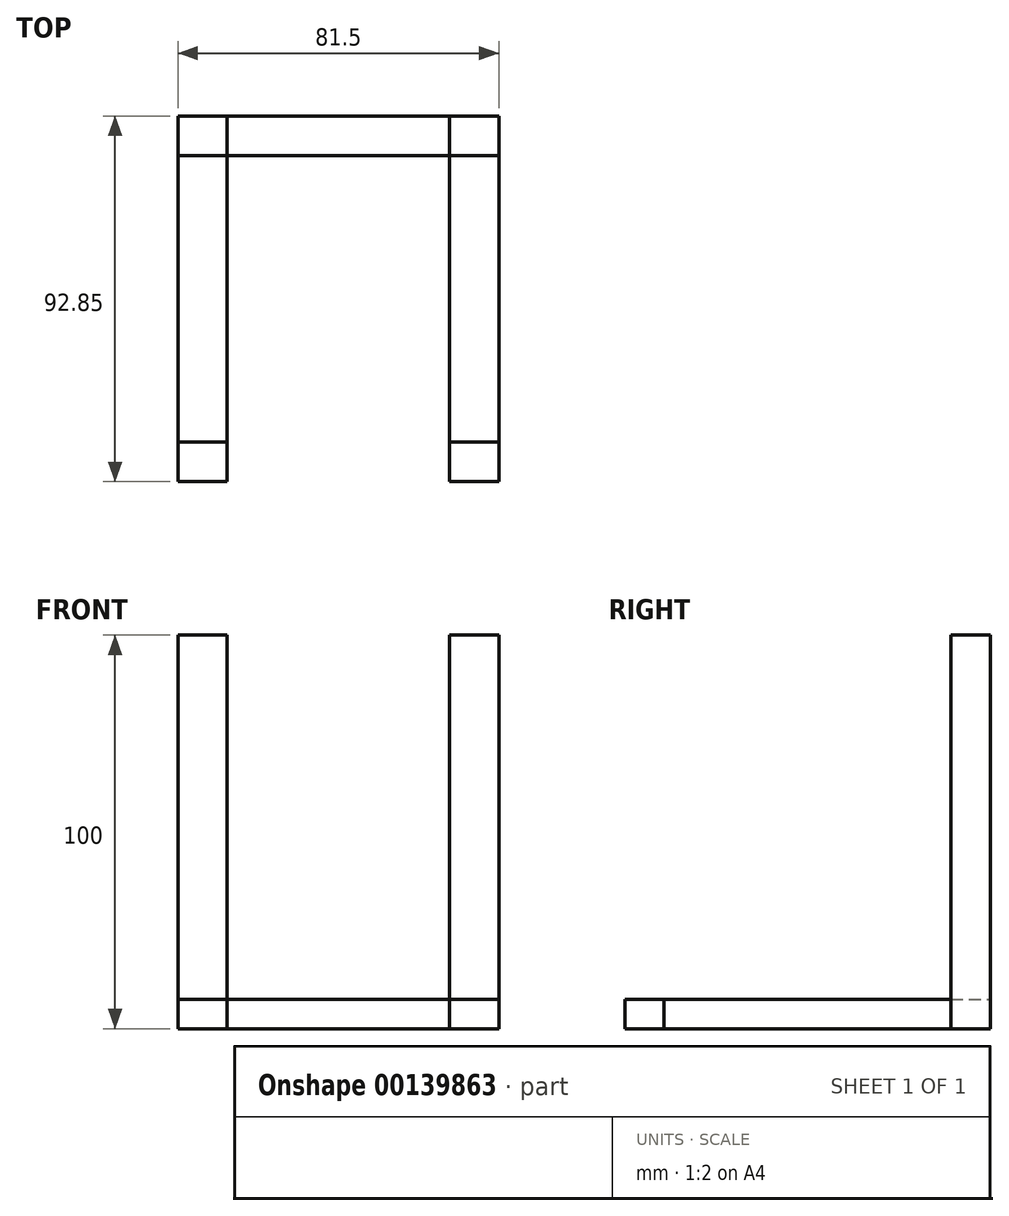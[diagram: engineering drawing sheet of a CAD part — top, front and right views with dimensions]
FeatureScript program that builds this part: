
annotation { "Feature Type Name" : "Feature", "Feature Type Description" : "" }
export const myFeature = defineFeature(function(context is Context, id is Id, definition is map)
    precondition{}
    {
        {
            var Q0;
            Q0=qCreatedBy(makeId("Top.planeOp"),FACE);
            var sketch = newSketch(context, id + "F0", { "sketchPlane" : qUnion([Q0])});
            skLineSegment(sketch, "E0", {"start": v(-34.4, 34.84) * mm, "end": v(47.1, 34.84) * mm});
            skLineSegment(sketch, "E1", {"start": v(47.1, 34.84) * mm, "end": v(47.1, -58.01) * mm});
            skLineSegment(sketch, "E2", {"start": v(47.1, -58.01) * mm, "end": v(-34.4, -58.01) * mm});
            skLineSegment(sketch, "E3", {"start": v(-34.4, -58.01) * mm, "end": v(-34.4, 34.84) * mm});
            skLineSegment(sketch, "E4", {"start": v(-34.4, 24.84) * mm, "end": v(-21.9, 24.84) * mm});
            skLineSegment(sketch, "E5", {"start": v(-21.9, 24.84) * mm, "end": v(-21.9, 34.84) * mm});
            skLineSegment(sketch, "E6", {"start": v(34.6, 34.84) * mm, "end": v(34.6, 24.84) * mm});
            skLineSegment(sketch, "E7", {"start": v(34.6, 24.84) * mm, "end": v(47.1, 24.84) * mm});
            skLineSegment(sketch, "E8", {"start": v(47.1, -48.01) * mm, "end": v(34.6, -48.01) * mm});
            skLineSegment(sketch, "E9", {"start": v(34.6, -48.01) * mm, "end": v(34.6, -58.01) * mm});
            skLineSegment(sketch, "E10", {"start": v(-34.4, -48.01) * mm, "end": v(-21.9, -48.01) * mm});
            skLineSegment(sketch, "E11", {"start": v(-21.9, -48.01) * mm, "end": v(-21.9, -58.01) * mm});
            skLineSegment(sketch, "E12", {"start": v(-21.9, 24.84) * mm, "end": v(-21.9, -48.01) * mm});
            skLineSegment(sketch, "E13", {"start": v(34.6, -48.01) * mm, "end": v(34.6, 24.84) * mm});
            skLineSegment(sketch, "E14", {"start": v(-21.9, 24.84) * mm, "end": v(34.6, 24.84) * mm});
            skSolve(sketch);
        }
        {
            var Q0;
            {var subQ4=sQuery(id+"F0.wireOp",EDGE,"E4");Q0=makeQuery(id+"F0.imprint","IMPRINT",FACE,{"disambiguationData":[TD([[makeQuery(id+"F0.imprint","IMPRINT",EDGE,{"derivedFrom":subQ4}),1.0]])]});}
            var Q1;
            {var subQ3=sQuery(id+"F0.wireOp",EDGE,"E6");Q1=makeQuery(id+"F0.imprint","IMPRINT",FACE,{"disambiguationData":[TD([[makeQuery(id+"F0.imprint","IMPRINT",EDGE,{"derivedFrom":subQ3}),1.0]])]});}
            extrude(context, id + "F1", {"entities" : qUnion([Q0, Q1]), "depth" : 100 * mm});
        }
        {
            var Q0;
            {var subQ0=sQuery(id+"F0.wireOp",EDGE,"E4");Q0=makeQuery(id+"F0.imprint","IMPRINT",FACE,{"disambiguationData":[TD([[makeQuery(id+"F0.imprint","IMPRINT",EDGE,{"derivedFrom":subQ0}),-1.0]])]});}
            var Q1;
            {var subQ0=sQuery(id+"F0.wireOp",EDGE,"E7");Q1=makeQuery(id+"F0.imprint","IMPRINT",FACE,{"disambiguationData":[TD([[makeQuery(id+"F0.imprint","IMPRINT",EDGE,{"derivedFrom":subQ0}),-1.0]])]});}
            var Q2;
            {var subQ0=sQuery(id+"F0.wireOp",EDGE,"E5");Q2=makeQuery(id+"F0.imprint","IMPRINT",FACE,{"disambiguationData":[TD([[makeQuery(id+"F0.imprint","IMPRINT",EDGE,{"derivedFrom":subQ0}),-1.0]])]});}
            extrude(context, id + "F2", {"entities" : qUnion([Q0, Q1, Q2]), "depth" : 7.5 * mm});
        }
        {
            var Q0;
            {var subQ4=sQuery(id+"F0.wireOp",EDGE,"E10");Q0=makeQuery(id+"F0.imprint","IMPRINT",FACE,{"disambiguationData":[TD([[makeQuery(id+"F0.imprint","IMPRINT",EDGE,{"derivedFrom":subQ4}),-1.0]])]});}
            var Q1;
            {var subQ3=sQuery(id+"F0.wireOp",EDGE,"E8");Q1=makeQuery(id+"F0.imprint","IMPRINT",FACE,{"disambiguationData":[TD([[makeQuery(id+"F0.imprint","IMPRINT",EDGE,{"derivedFrom":subQ3}),1.0]])]});}
            extrude(context, id + "F3", {"entities" : qUnion([Q0, Q1]), "depth" : 7.5 * mm});
        }
    });
